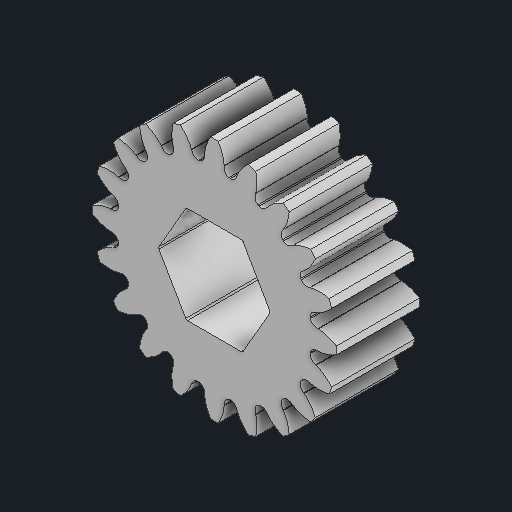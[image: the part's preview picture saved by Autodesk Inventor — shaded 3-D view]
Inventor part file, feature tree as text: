
AUTODESK INVENTOR PART (.ipt)
format: ipt  version: 2024.2 (Build 282272000, 272)  size: 1,250,304 bytes
history: native  units: in
note: dims shown in document units (in); Inventor stores cm internally (conversion verified against a paired STEP export)
features: extrude x3, sketch x3, other x2
ambient origin geometry x8: Origin, YZ Plane, XZ Plane, XY Plane, X Axis, Y Axis, Z Axis, Center Point
bodies: Solid1 (feature_tree), Solid2 (feature_tree), Solid3 (feature_tree)
feature tree (8):
  extrude  "Extrusion1"  TaperAngle=0.0deg  [1 undecoded]
  extrude  "Extrusion2"  Depth=1.0in TaperAngle=0.0deg
  extrude  "Extrusion3"  Depth=1.0in TaperAngle=0.0deg
  sketch  "Sketch1"  dims[d0=1.0in d1=0.0in d2=0.0in]
  sketch  "Sketch2"  dims[d3=0.25in d4=1.0in d5=0.0in]
  sketch  "Sketch3"  dims[d6=0.25in d7=1.0in d8=0.0in]
  other  "2806-0005-0004_91390A117_2:1"
  other  "2806-0005-0004_91390A117_3:1"
note: 1 required parameter value undecoded (feature->parameter linkage not recoverable at this tier; creation-order binding heuristic only, values carry confidence <= 0.55)
